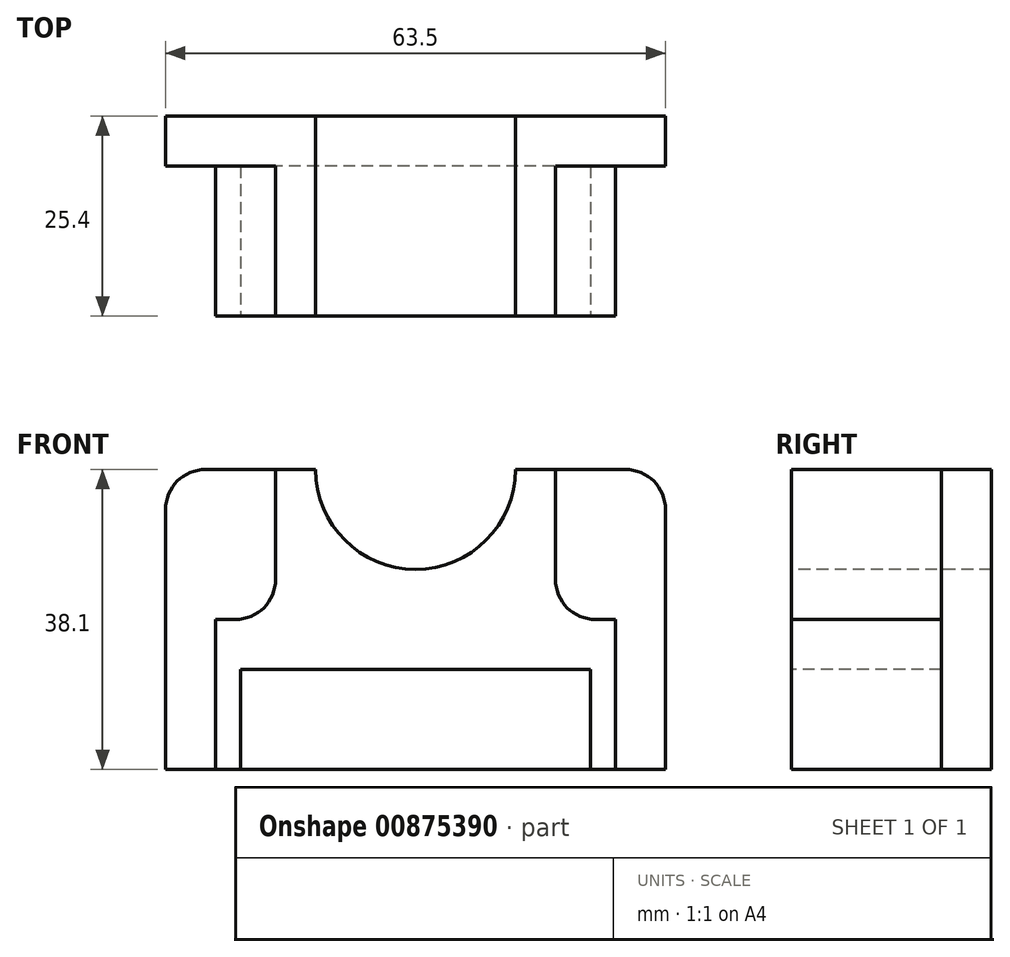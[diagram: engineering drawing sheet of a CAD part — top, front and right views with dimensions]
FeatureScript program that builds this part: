
annotation { "Feature Type Name" : "Feature", "Feature Type Description" : "" }
export const myFeature = defineFeature(function(context is Context, id is Id, definition is map)
    precondition{}
    {
        {
            var Q0;
            Q0=qCreatedBy(makeId("Front.planeOp"),FACE);
            var sketch = newSketch(context, id + "F0", { "sketchPlane" : qUnion([Q0])});
            skLineSegment(sketch, "E0.bottom", {"start": v(31.75, -19.05) * mm, "end": v(-31.75, -19.05) * mm});
            skLineSegment(sketch, "E0.top", {"start": v(31.75, 19.05) * mm, "end": v(-31.75, 19.05) * mm});
            skLineSegment(sketch, "E0.left", {"start": v(31.75, -19.05) * mm, "end": v(31.75, 19.05) * mm});
            skLineSegment(sketch, "E0.right", {"start": v(-31.75, -19.05) * mm, "end": v(-31.75, 19.05) * mm});
            skPoint(sketch, "E0.middle", {"position": v(0, 0) * mm});
            skSolve(sketch);
        }
        {
            var Q0;
            Q0=makeQuery(id+"F0.imprint","IMPRINT",FACE,{"disambiguationData":[TD([[makeQuery(id+"F0.imprint","IMPRINT",EDGE,{"derivedFrom":sQuery(id+"F0.wireOp",EDGE,"E0.bottom")}),-1.0]])]});
            extrude(context, id + "F1", {"entities" : qUnion([Q0]), "depth" : 25.4 * mm, "offsetDistance" : 25.4 * mm});
        }
        {
            var Q0;
            Q0=makeQuery(id+"F1.opExtrude","CAP_FACE",FACE,{"disambiguationData":[OSD([sQuery(id+"F0.wireOp",EDGE,"E0.bottom"),sQuery(id+"F0.wireOp",EDGE,"E0.top"),sQuery(id+"F0.wireOp",EDGE,"E0.left"),sQuery(id+"F0.wireOp",EDGE,"E0.right")])],"isStart":false});
            var sketch = newSketch(context, id + "F2", { "sketchPlane" : qUnion([Q0])});
            skArc(sketch, "E1", {"start": v(-12.7, 19.05) * mm, "mid": v(0, 6.35) * mm, "end": v(12.7, 19.05) * mm});
            skSolve(sketch);
        }
        {
            var Q0;
            Q0 = qSketchRegion(id + "F2", true);
            var Q1;
            {var subQ0=sQuery(id+"F2.wireOp",EDGE,"E1");Q1=makeQuery(id+"F2.imprint","IMPRINT",FACE,{"disambiguationData":[TD([[makeQuery(id+"F2.imprint","IMPRINT",EDGE,{"derivedFrom":subQ0}),1.0]])]});}
            extrude(context, id + "F3", {"entities" : qUnion([Q0, Q1]), "operationType" : NewBodyOperationType.REMOVE, "oppositeDirection" : true, "depth" : 38.1 * mm, "offsetDistance" : 25.4 * mm});
        }
        {
            var Q0;
            Q0=makeQuery(id+"F1.opExtrude","CAP_FACE",FACE,{"disambiguationData":[OSD([sQuery(id+"F0.wireOp",EDGE,"E0.bottom"),sQuery(id+"F0.wireOp",EDGE,"E0.top"),sQuery(id+"F0.wireOp",EDGE,"E0.left"),sQuery(id+"F0.wireOp",EDGE,"E0.right")])],"isStart":false});
            var sketch = newSketch(context, id + "F4", { "sketchPlane" : qUnion([Q0])});
            skLineSegment(sketch, "E2.bottom", {"start": v(-22.23, -19.05) * mm, "end": v(22.22, -19.05) * mm});
            skLineSegment(sketch, "E2.top", {"start": v(-22.23, -6.35) * mm, "end": v(22.23, -6.35) * mm});
            skLineSegment(sketch, "E2.left", {"start": v(-22.23, -19.05) * mm, "end": v(-22.23, -6.35) * mm});
            skLineSegment(sketch, "E2.right", {"start": v(22.22, -19.05) * mm, "end": v(22.22, -6.35) * mm});
            skPoint(sketch, "E2.middle", {"position": v(0, -12.7) * mm});
            skSolve(sketch);
        }
        {
            var Q0;
            Q0=makeQuery(id+"F4.imprint","IMPRINT",FACE,{"disambiguationData":[TD([[makeQuery(id+"F4.imprint","IMPRINT",EDGE,{"derivedFrom":sQuery(id+"F4.wireOp",EDGE,"E2.bottom")}),-1.0]])]});
            extrude(context, id + "F5", {"entities" : qUnion([Q0]), "operationType" : NewBodyOperationType.REMOVE, "oppositeDirection" : true, "depth" : 19.05 * mm, "offsetDistance" : 25.4 * mm});
        }
        {
            var Q0;
            Q0=makeQuery(id+"F1.opExtrude","CAP_FACE",FACE,{"disambiguationData":[OSD([sQuery(id+"F0.wireOp",EDGE,"E0.bottom"),sQuery(id+"F0.wireOp",EDGE,"E0.top"),sQuery(id+"F0.wireOp",EDGE,"E0.left"),sQuery(id+"F0.wireOp",EDGE,"E0.right")])],"isStart":false});
            var sketch = newSketch(context, id + "F6", { "sketchPlane" : qUnion([Q0])});
            skLineSegment(sketch, "E3.bottom", {"start": v(-31.75, 19.05) * mm, "end": v(-25.4, 19.05) * mm});
            skLineSegment(sketch, "E3.top", {"start": v(-31.75, -19.05) * mm, "end": v(-25.4, -19.05) * mm});
            skLineSegment(sketch, "E3.left", {"start": v(-31.75, 19.05) * mm, "end": v(-31.75, -19.05) * mm});
            skLineSegment(sketch, "E3.right", {"start": v(-25.4, 19.05) * mm, "end": v(-25.4, -19.05) * mm});
            skSolve(sketch);
        }
        {
            var Q0;
            Q0=makeQuery(id+"F6.imprint","IMPRINT",FACE,{"disambiguationData":[TD([[makeQuery(id+"F6.imprint","IMPRINT",EDGE,{"derivedFrom":sQuery(id+"F6.wireOp",EDGE,"E3.bottom")}),1.0]])]});
            extrude(context, id + "F7", {"entities" : qUnion([Q0]), "operationType" : NewBodyOperationType.REMOVE, "oppositeDirection" : true, "depth" : 19.05 * mm, "offsetDistance" : 25.4 * mm});
        }
        {
            var Q0;
            Q0=makeQuery(id+"F1.opExtrude","CAP_FACE",FACE,{"disambiguationData":[OSD([sQuery(id+"F0.wireOp",EDGE,"E0.bottom"),sQuery(id+"F0.wireOp",EDGE,"E0.top"),sQuery(id+"F0.wireOp",EDGE,"E0.left"),sQuery(id+"F0.wireOp",EDGE,"E0.right")])],"isStart":false});
            var sketch = newSketch(context, id + "F8", { "sketchPlane" : qUnion([Q0])});
            skLineSegment(sketch, "E4.bottom", {"start": v(31.75, 19.05) * mm, "end": v(25.4, 19.05) * mm});
            skLineSegment(sketch, "E4.top", {"start": v(31.75, -19.05) * mm, "end": v(25.4, -19.05) * mm});
            skLineSegment(sketch, "E4.left", {"start": v(31.75, 19.05) * mm, "end": v(31.75, -19.05) * mm});
            skLineSegment(sketch, "E4.right", {"start": v(25.4, 19.05) * mm, "end": v(25.4, -19.05) * mm});
            skSolve(sketch);
        }
        {
            var Q0;
            Q0=makeQuery(id+"F8.imprint","IMPRINT",FACE,{"disambiguationData":[TD([[makeQuery(id+"F8.imprint","IMPRINT",EDGE,{"derivedFrom":sQuery(id+"F8.wireOp",EDGE,"E4.bottom")}),1.0]])]});
            extrude(context, id + "F9", {"entities" : qUnion([Q0]), "operationType" : NewBodyOperationType.REMOVE, "oppositeDirection" : true, "depth" : 19.05 * mm, "offsetDistance" : 25.4 * mm});
        }
        {
            var Q0;
            Q0=makeQuery(id+"F1.opExtrude","SWEPT_EDGE",EDGE,{"disambiguationData":[OSD([sQuery(id+"F0.wireOp",EDGE,"E0.top"),sQuery(id+"F0.wireOp",EDGE,"E0.left")])]});
            var Q1;
            Q1=makeQuery(id+"F1.opExtrude","SWEPT_EDGE",EDGE,{"disambiguationData":[OSD([sQuery(id+"F0.wireOp",EDGE,"E0.top"),sQuery(id+"F0.wireOp",EDGE,"E0.right")])]});
            fillet(context, id + "F10", {"entities" : qUnion([Q0, Q1]), "radius" : 5.08 * mm, "tangentPropagation" : true, "allowEdgeOverflow" : false});
        }
        {
            var Q0;
            Q0=makeQuery(id+"F1.opExtrude","CAP_FACE",FACE,{"disambiguationData":[OSD([sQuery(id+"F0.wireOp",EDGE,"E0.bottom"),sQuery(id+"F0.wireOp",EDGE,"E0.top"),sQuery(id+"F0.wireOp",EDGE,"E0.left"),sQuery(id+"F0.wireOp",EDGE,"E0.right")])],"isStart":false});
            var sketch = newSketch(context, id + "F11", { "sketchPlane" : qUnion([Q0])});
            skLineSegment(sketch, "E5.bottom", {"start": v(-25.4, 19.05) * mm, "end": v(-17.78, 19.05) * mm});
            skLineSegment(sketch, "E5.top", {"start": v(-25.4, 0) * mm, "end": v(-17.78, 0) * mm});
            skLineSegment(sketch, "E5.left", {"start": v(-25.4, 19.05) * mm, "end": v(-25.4, 0) * mm});
            skLineSegment(sketch, "E5.right", {"start": v(-17.78, 19.05) * mm, "end": v(-17.78, 0) * mm});
            skSolve(sketch);
        }
        {
            var Q0;
            Q0=makeQuery(id+"F11.imprint","IMPRINT",FACE,{"disambiguationData":[TD([[makeQuery(id+"F11.imprint","IMPRINT",EDGE,{"derivedFrom":sQuery(id+"F11.wireOp",EDGE,"E5.bottom")}),1.0]])]});
            extrude(context, id + "F12", {"entities" : qUnion([Q0]), "operationType" : NewBodyOperationType.REMOVE, "oppositeDirection" : true, "depth" : 19.05 * mm, "offsetDistance" : 25.4 * mm});
        }
        {
            var Q0;
            Q0=makeQuery(id+"F12.boolean.opBoolean","COPY",EDGE,{"derivedFrom":makeQuery(id+"F12.opExtrude","SWEPT_EDGE",EDGE,{"disambiguationData":[OSD([sQuery(id+"F11.wireOp",EDGE,"E5.top"),sQuery(id+"F11.wireOp",EDGE,"E5.right")])]})});
            fillet(context, id + "F13", {"entities" : qUnion([Q0]), "radius" : 5.08 * mm, "tangentPropagation" : true, "allowEdgeOverflow" : false});
        }
        {
            var Q0;
            Q0=makeQuery(id+"F1.opExtrude","CAP_FACE",FACE,{"disambiguationData":[OSD([sQuery(id+"F0.wireOp",EDGE,"E0.bottom"),sQuery(id+"F0.wireOp",EDGE,"E0.top"),sQuery(id+"F0.wireOp",EDGE,"E0.left"),sQuery(id+"F0.wireOp",EDGE,"E0.right")])],"isStart":false});
            var sketch = newSketch(context, id + "F14", { "sketchPlane" : qUnion([Q0])});
            skLineSegment(sketch, "E6.bottom", {"start": v(25.4, 19.05) * mm, "end": v(17.78, 19.05) * mm});
            skLineSegment(sketch, "E6.top", {"start": v(25.4, 0) * mm, "end": v(17.78, 0) * mm});
            skLineSegment(sketch, "E6.left", {"start": v(25.4, 19.05) * mm, "end": v(25.4, 0) * mm});
            skLineSegment(sketch, "E6.right", {"start": v(17.78, 19.05) * mm, "end": v(17.78, 0) * mm});
            skSolve(sketch);
        }
        {
            var Q0;
            Q0=makeQuery(id+"F14.imprint","IMPRINT",FACE,{"disambiguationData":[TD([[makeQuery(id+"F14.imprint","IMPRINT",EDGE,{"derivedFrom":sQuery(id+"F14.wireOp",EDGE,"E6.bottom")}),1.0]])]});
            extrude(context, id + "F15", {"entities" : qUnion([Q0]), "operationType" : NewBodyOperationType.REMOVE, "oppositeDirection" : true, "depth" : 19.05 * mm, "offsetDistance" : 25.4 * mm});
        }
        {
            var Q0;
            Q0=makeQuery(id+"F15.boolean.opBoolean","COPY",EDGE,{"derivedFrom":makeQuery(id+"F15.opExtrude","SWEPT_EDGE",EDGE,{"disambiguationData":[OSD([sQuery(id+"F14.wireOp",EDGE,"E6.top"),sQuery(id+"F14.wireOp",EDGE,"E6.right")])]})});
            fillet(context, id + "F16", {"entities" : qUnion([Q0]), "radius" : 5.08 * mm, "tangentPropagation" : true, "allowEdgeOverflow" : false});
        }
    });
